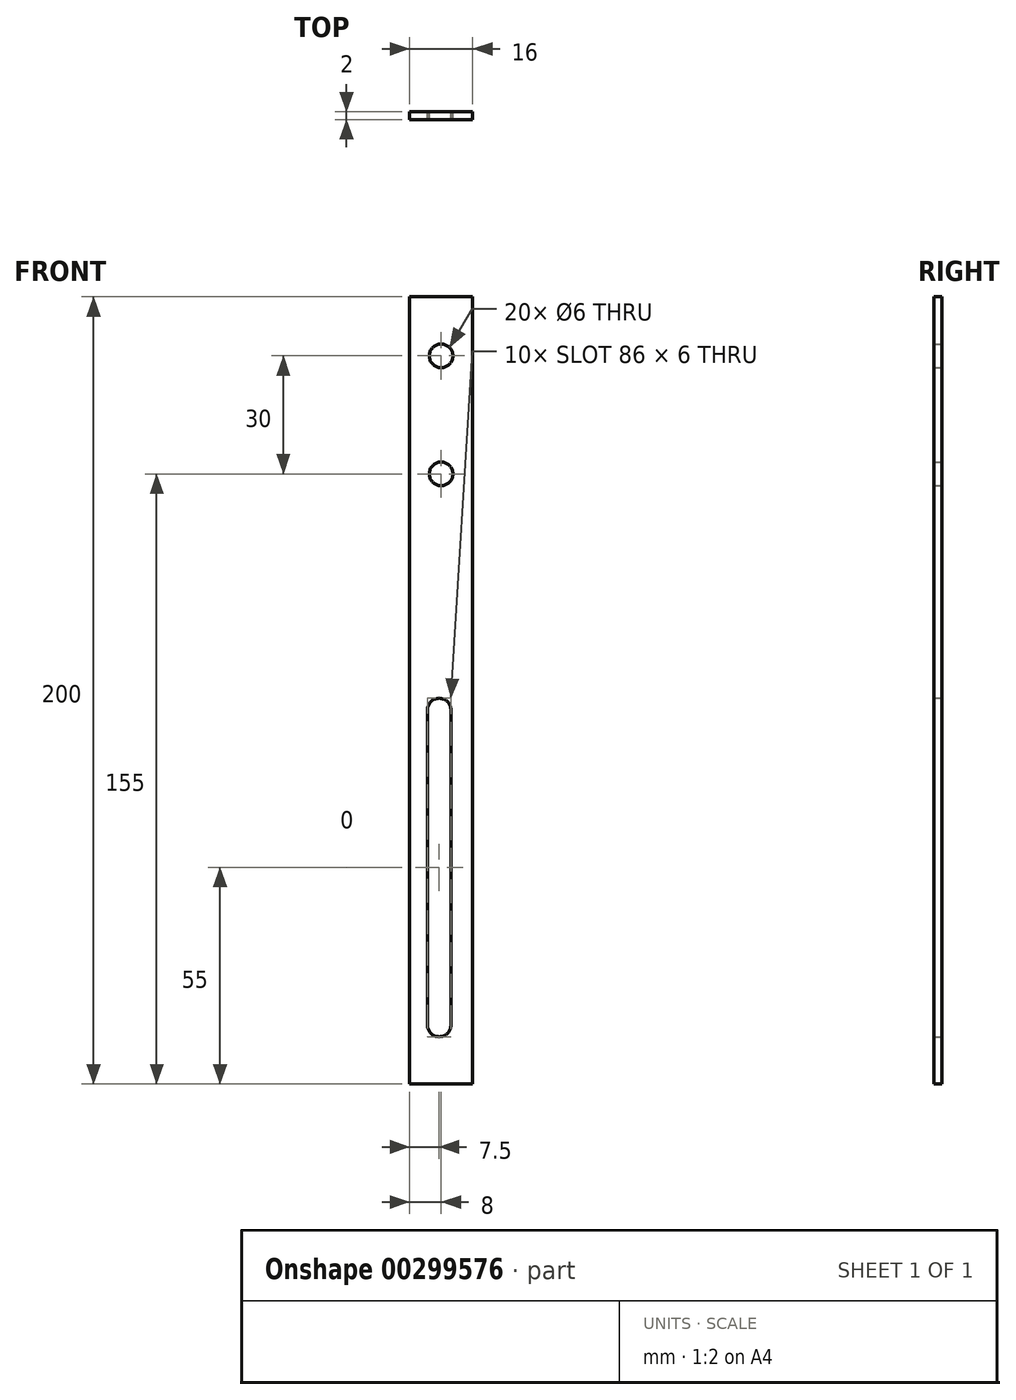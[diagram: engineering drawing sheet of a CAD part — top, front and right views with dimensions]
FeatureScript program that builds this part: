
annotation { "Feature Type Name" : "Feature", "Feature Type Description" : "" }
export const myFeature = defineFeature(function(context is Context, id is Id, definition is map)
    precondition{}
    {
        {
            var Q0;
            Q0=qCreatedBy(makeId("Front.planeOp"),FACE);
            var sketch = newSketch(context, id + "F0", { "sketchPlane" : qUnion([Q0])});
            skLineSegment(sketch, "E0.bottom", {"start": v(0, 0) * mm, "end": v(16, 0) * mm});
            skLineSegment(sketch, "E0.top", {"start": v(0, 200) * mm, "end": v(16, 200) * mm});
            skLineSegment(sketch, "E0.left", {"start": v(0, 0) * mm, "end": v(0, 200) * mm});
            skLineSegment(sketch, "E0.right", {"start": v(16, 0) * mm, "end": v(16, 200) * mm});
            skCircle(sketch, "E1", {"center": v(8, 185) * mm, "radius": 3 * mm});
            skPoint(sketch, "E2", {"position": v(8, 200) * mm});
            skCircle(sketch, "E3.0.1.0", {"center": v(8, 155) * mm, "radius": 3 * mm});
            skLineSegment(sketch, "E3.direction1", {"start": v(8, 185) * mm, "end": v(32.5, 185) * mm, "construction": true});
            skLineSegment(sketch, "E3.direction2", {"start": v(8, 185) * mm, "end": v(8, 155) * mm, "construction": true});
            skLineSegment(sketch, "E4", {"start": v(4.5, 95) * mm, "end": v(4.5, 15) * mm});
            skLineSegment(sketch, "E5", {"start": v(10.5, 95) * mm, "end": v(10.5, 15) * mm});
            skArc(sketch, "E6", {"start": v(4.5, 15) * mm, "mid": v(7.5, 12) * mm, "end": v(10.5, 15) * mm});
            skArc(sketch, "E7", {"start": v(10.5, 95) * mm, "mid": v(7.5, 98) * mm, "end": v(4.5, 95) * mm});
            skSolve(sketch);
        }
        {
            var Q0;
            Q0 = qSketchRegion(id + "F0", true);
            extrude(context, id + "F1", {"entities" : qUnion([Q0]), "depth" : 2 * mm});
        }
    });
